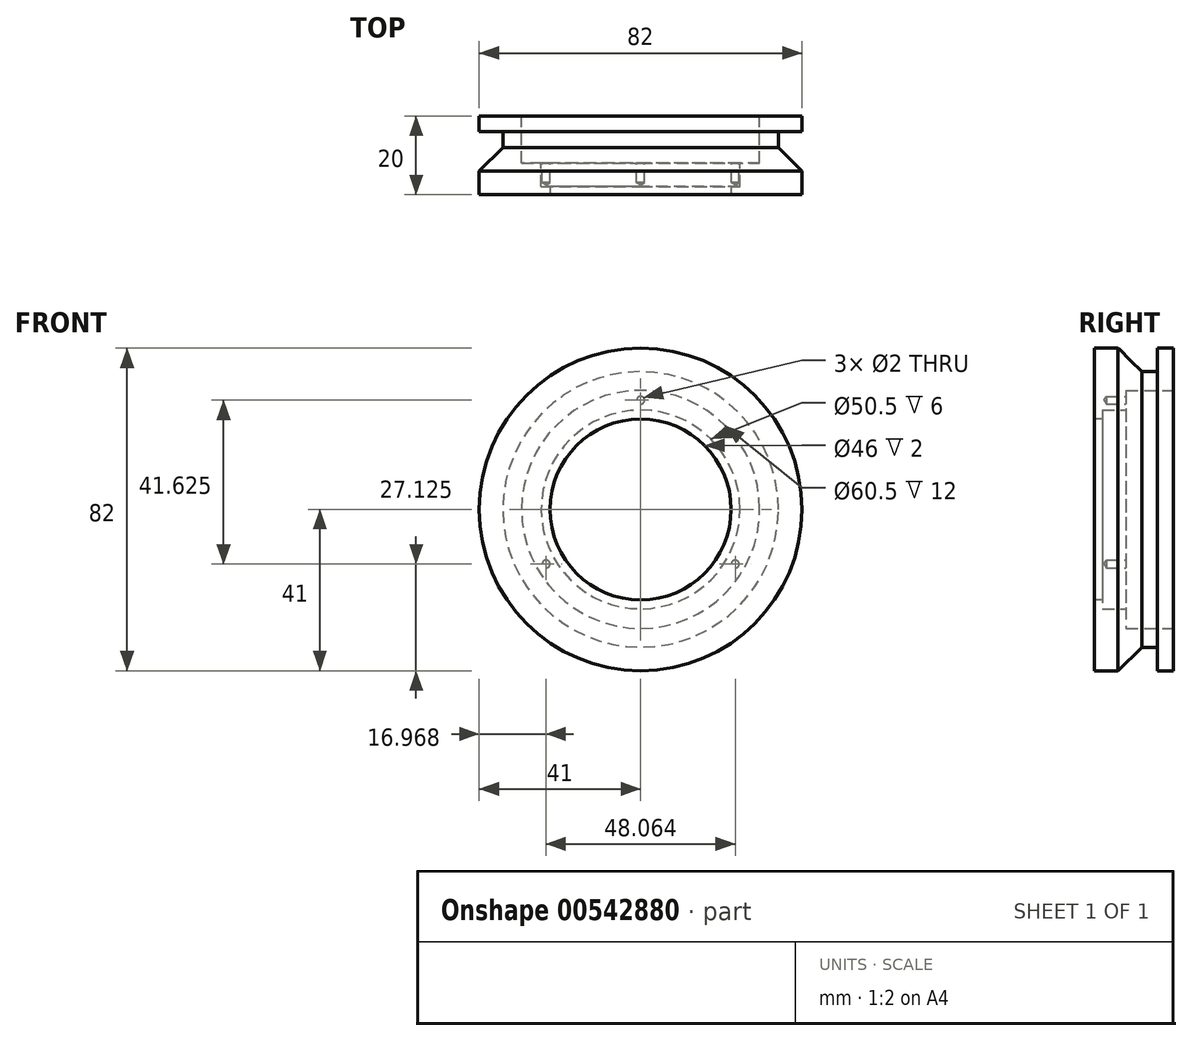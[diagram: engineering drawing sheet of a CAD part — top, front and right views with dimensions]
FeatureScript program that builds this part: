
annotation { "Feature Type Name" : "Feature", "Feature Type Description" : "" }
export const myFeature = defineFeature(function(context is Context, id is Id, definition is map)
    precondition{}
    {
        {
            var Q0;
            Q0=qCreatedBy(makeId("Right.planeOp"),FACE);
            var sketch = newSketch(context, id + "F0", { "sketchPlane" : qUnion([Q0])});
            skLineSegment(sketch, "E0", {"start": v(0, 0) * mm, "end": v(0, 41) * mm});
            skLineSegment(sketch, "E1", {"start": v(0, 41) * mm, "end": v(6, 41) * mm});
            skLineSegment(sketch, "E2", {"start": v(6, 41) * mm, "end": v(12, 35) * mm});
            skLineSegment(sketch, "E3", {"start": v(16, 41) * mm, "end": v(20, 41) * mm});
            skLineSegment(sketch, "E4", {"start": v(20, 41) * mm, "end": v(20, 0) * mm});
            skLineSegment(sketch, "E5", {"start": v(20, 0) * mm, "end": v(0, 0) * mm});
            skLineSegment(sketch, "E6", {"start": v(12, 35) * mm, "end": v(16, 35) * mm});
            skLineSegment(sketch, "E7", {"start": v(16, 35) * mm, "end": v(16, 41) * mm});
            skSolve(sketch);
        }
        {
            var Q0;
            Q0=makeQuery(id+"F0.imprint","IMPRINT",FACE,{"disambiguationData":[TD([[makeQuery(id+"F0.imprint","IMPRINT",EDGE,{"derivedFrom":sQuery(id+"F0.wireOp",EDGE,"E0")}),-1.0]])]});
            var Q1;
            Q1=sQuery(id+"F0.wireOp",EDGE,"E5");
            revolve(context, id + "F1", {"entities" : qUnion([Q0]), "axis" : qUnion([Q1]), "revolveType" : RevolveType.FULL});
        }
        {
            var Q0;
            Q0=makeQuery(id+"F1.opRevolve","SWEPT_FACE",FACE,{"disambiguationData":[OSD([sQuery(id+"F0.wireOp",EDGE,"E4")])]});
            var sketch = newSketch(context, id + "F2", { "sketchPlane" : qUnion([Q0])});
            skCircle(sketch, "E8", {"center": v(0, 0) * mm, "radius": 25.25 * mm});
            skSolve(sketch);
        }
        {
            var Q0;
            Q0=makeQuery(id+"F2.imprint","IMPRINT",FACE,{"disambiguationData":[TD([[makeQuery(id+"F2.imprint","IMPRINT",EDGE,{"derivedFrom":sQuery(id+"F2.wireOp",EDGE,"E8")}),1.0]])]});
            extrude(context, id + "F3", {"entities" : qUnion([Q0]), "operationType" : NewBodyOperationType.REMOVE, "oppositeDirection" : true, "depth" : 18 * mm, "offsetDistance" : 25 * mm});
        }
        {
            var Q0;
            Q0=makeQuery(id+"F1.opRevolve","SWEPT_FACE",FACE,{"disambiguationData":[OSD([sQuery(id+"F0.wireOp",EDGE,"E0")])]});
            var sketch = newSketch(context, id + "F4", { "sketchPlane" : qUnion([Q0])});
            skCircle(sketch, "E9", {"center": v(0, 0) * mm, "radius": 23 * mm});
            skSolve(sketch);
        }
        {
            var Q0;
            Q0=makeQuery(id+"F4.imprint","IMPRINT",FACE,{"disambiguationData":[TD([[makeQuery(id+"F4.imprint","IMPRINT",EDGE,{"derivedFrom":sQuery(id+"F4.wireOp",EDGE,"E9")}),1.0]])]});
            extrude(context, id + "F5", {"entities" : qUnion([Q0]), "operationType" : NewBodyOperationType.REMOVE, "endBound" : BoundingType.UP_TO_NEXT, "oppositeDirection" : true, "depth" : 25 * mm, "offsetDistance" : 25 * mm});
        }
        {
            var Q0;
            Q0=makeQuery(id+"F1.opRevolve","SWEPT_FACE",FACE,{"disambiguationData":[OSD([sQuery(id+"F0.wireOp",EDGE,"E4")])]});
            var sketch = newSketch(context, id + "F6", { "sketchPlane" : qUnion([Q0])});
            skCircle(sketch, "E10", {"center": v(0, 0) * mm, "radius": 30.25 * mm});
            skSolve(sketch);
        }
        {
            var Q0;
            Q0=makeQuery(id+"F6.imprint","IMPRINT",FACE,{"disambiguationData":[TD([[makeQuery(id+"F6.imprint","IMPRINT",EDGE,{"derivedFrom":sQuery(id+"F6.wireOp",EDGE,"E10")}),1.0]])]});
            extrude(context, id + "F7", {"entities" : qUnion([Q0]), "operationType" : NewBodyOperationType.REMOVE, "oppositeDirection" : true, "depth" : 12 * mm, "offsetDistance" : 25 * mm});
        }
        {
            var Q0;
            Q0=makeQuery(id+"F7.boolean.opBoolean","COPY",FACE,{"derivedFrom":makeQuery(id+"F7.opExtrude","CAP_FACE",FACE,{"disambiguationData":[OSD([sQuery(id+"F2.wireOp",EDGE,"E8"),sQuery(id+"F6.wireOp",EDGE,"E10")])],"isStart":false})});
            var sketch = newSketch(context, id + "F8", { "sketchPlane" : qUnion([Q0])});
            skLineSegment(sketch, "E11", {"start": v(0, 30.25) * mm, "end": v(0, 25.25) * mm, "construction": true});
            skPoint(sketch, "E12", {"position": v(0, 27.75) * mm});
            skPoint(sketch, "E13.1.0", {"position": v(-24.03, -13.87) * mm});
            skPoint(sketch, "E13.2.0", {"position": v(24.03, -13.88) * mm});
            skPoint(sketch, "E13.center", {"position": v(0, 0) * mm});
            skSolve(sketch);
        }
        {
            var Q0;
            Q0=sQuery(id+"F8.wireOp",VERTEX,"E12");
            var Q1;
            Q1=sQuery(id+"F8.wireOp",VERTEX,"E13.2.0");
            var Q2;
            Q2=sQuery(id+"F8.wireOp",VERTEX,"E13.1.0");
            var Q3;
            Q3=makeQuery(id+"F1.opRevolve","SWEPT_BODY",BODY,{"disambiguationData":[OSD([sQuery(id+"F0.wireOp",EDGE,"E0"),sQuery(id+"F0.wireOp",EDGE,"E1"),sQuery(id+"F0.wireOp",EDGE,"E2"),sQuery(id+"F0.wireOp",EDGE,"E3"),sQuery(id+"F0.wireOp",EDGE,"E4"),sQuery(id+"F0.wireOp",EDGE,"E5"),sQuery(id+"F0.wireOp",EDGE,"E6"),sQuery(id+"F0.wireOp",EDGE,"E7")])]});
            hole(context, id + "F9", {"style" : HoleStyle.SIMPLE, "endStyle" : HoleEndStyle.BLIND, "holeDiameter" : 2 * mm, "holeDepth" : 5 * mm, "isTappedThrough" : true, "tappedDepth" : 6.5 * mm, "tapClearance" : 3, "locations" : qUnion([Q0, Q1, Q2]), "scope" : qUnion([Q3])});
        }
    });
